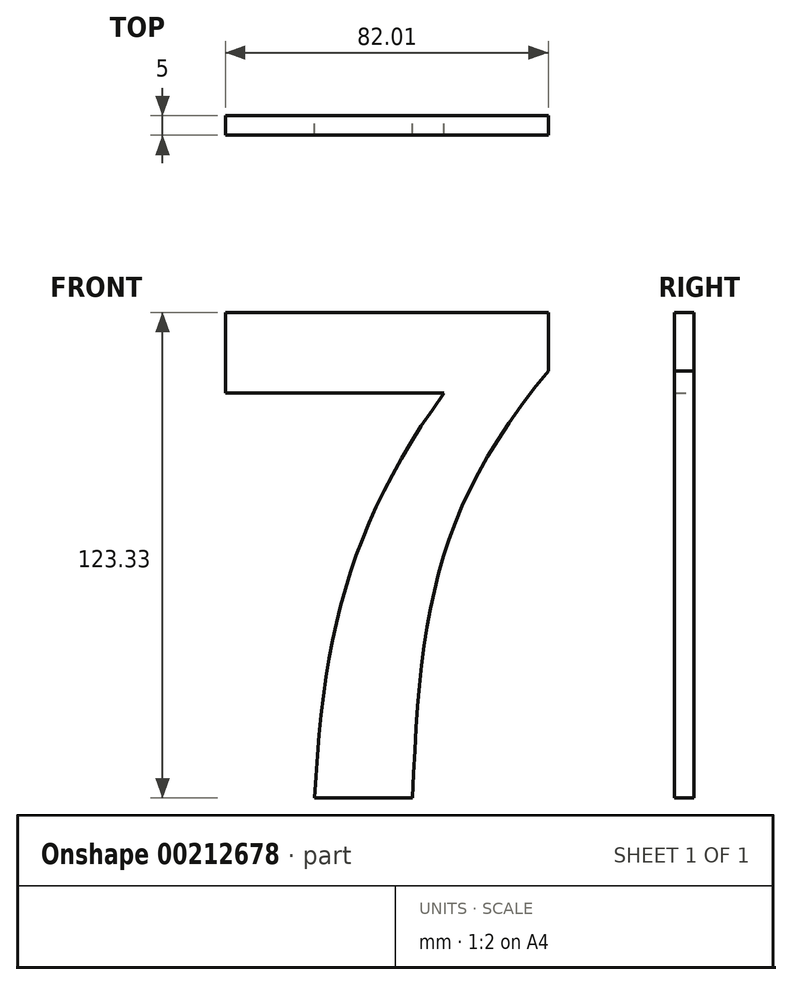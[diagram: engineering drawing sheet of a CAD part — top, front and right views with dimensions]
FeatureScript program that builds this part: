
annotation { "Feature Type Name" : "Feature", "Feature Type Description" : "" }
export const myFeature = defineFeature(function(context is Context, id is Id, definition is map)
    precondition{}
    {
        {
            var Q0;
            Q0=qCreatedBy(makeId("Front.planeOp"),FACE);
            var sketch = newSketch(context, id + "F0", { "sketchPlane" : qUnion([Q0])});
            skText(sketch, "E0", { "text": "7", "fontName": "NotoSansCJKsc-Bold.otf"});
            const initialGuessF0  = {"E0": [-0.0561, -0.06256, 1, 0, 0.12]};
            skSetInitialGuess(sketch, initialGuessF0);
            skSolve(sketch);
        }
        {
            var Q0;
            Q0=makeQuery(id+"F0.imprint","IMPRINT",FACE,{"disambiguationData":[TD([[makeQuery(id+"F0.imprint","IMPRINT",EDGE,{"derivedFrom":sQuery(id+"F0.wireOp",EDGE,"E0.sketch_text.stroke-0")}),1.0]])]});
            extrude(context, id + "F1", {"entities" : qUnion([Q0]), "depth" : 5 * mm});
        }
    });
